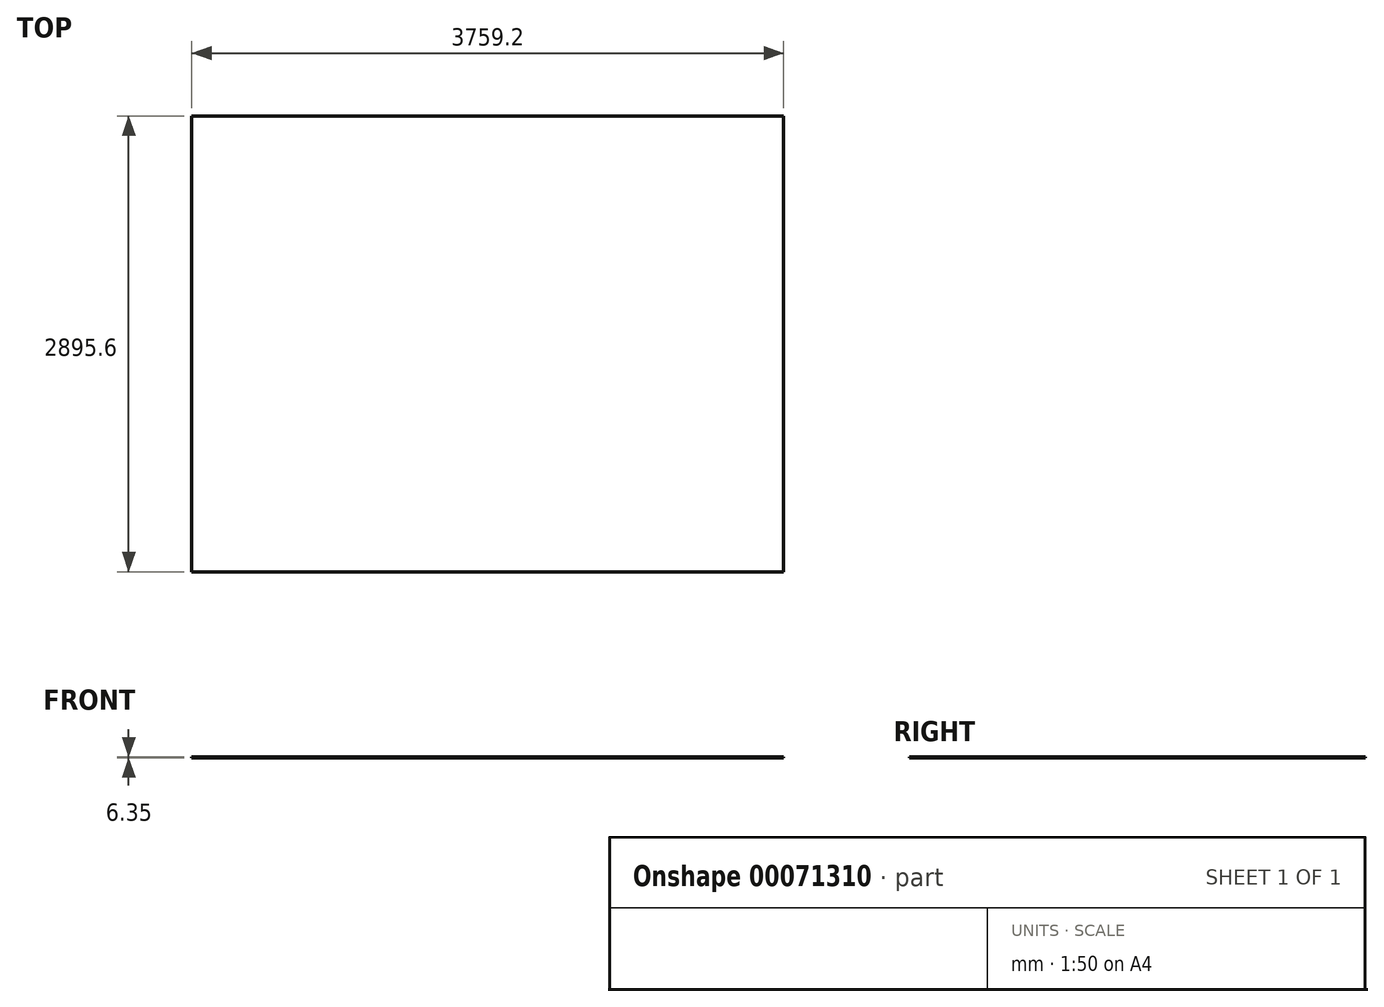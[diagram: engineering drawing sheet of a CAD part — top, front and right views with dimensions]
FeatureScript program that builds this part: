
annotation { "Feature Type Name" : "Feature", "Feature Type Description" : "" }
export const myFeature = defineFeature(function(context is Context, id is Id, definition is map)
    precondition{}
    {
        {
            var Q0;
            Q0=qCreatedBy(makeId("Top.planeOp"),FACE);
            var sketch = newSketch(context, id + "F0", { "sketchPlane" : qUnion([Q0])});
            skLineSegment(sketch, "E0.rect.bottom", {"start": v(1879.6, 1447.8) * mm, "end": v(-1879.6, 1447.8) * mm});
            skLineSegment(sketch, "E0.rect.top", {"start": v(1879.6, -1447.8) * mm, "end": v(-1879.6, -1447.8) * mm});
            skLineSegment(sketch, "E0.rect.left", {"start": v(1879.6, 1447.8) * mm, "end": v(1879.6, -1447.8) * mm});
            skLineSegment(sketch, "E0.rect.right", {"start": v(-1879.6, 1447.8) * mm, "end": v(-1879.6, -1447.8) * mm});
            skPoint(sketch, "E0.rect.middle", {"position": v(0, 0) * mm});
            skSolve(sketch);
        }
        {
            var Q0;
            Q0 = qSketchRegion(id + "F0", true);
            extrude(context, id + "F1", {"entities" : qUnion([Q0]), "depth" : 6.35 * mm});
        }
    });
